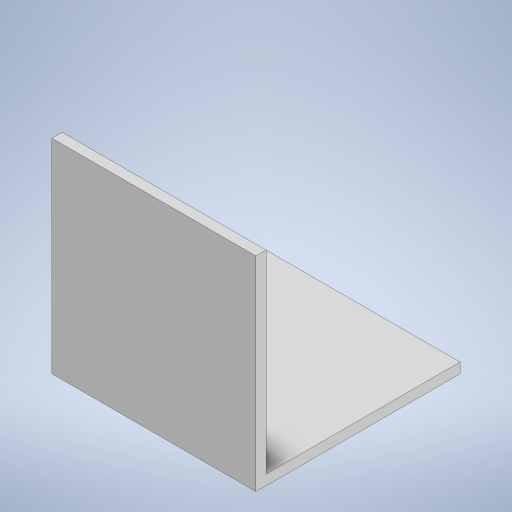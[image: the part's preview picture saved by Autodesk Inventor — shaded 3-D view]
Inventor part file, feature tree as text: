
AUTODESK INVENTOR PART (.ipt)
format: ipt  version: 2023.2 (Build 272271000, 271)  size: 219,136 bytes
history: native  units: mm
features: extrude x2, sketch x2, projected_geometry x1
ambient origin geometry x8: Origin, YZ Plane, XZ Plane, XY Plane, X Axis, Y Axis, Z Axis, Center Point
bodies: Solid1 (feature_tree)
feature tree (5):
  extrude  "Extrusion1"  Depth=60.0mm
  extrude  "Extrusion2"  Depth=60.0mm
  sketch  "Sketch1"  dims[d0=60.0mm d1=60.0mm]
  sketch  "Sketch2"  dims[d2=3.0mm d3=0.0mm d4=60.0mm d5=60.0mm d6=3.0mm d7=0.0mm]
  projected_geometry  "Projected Loop1"
